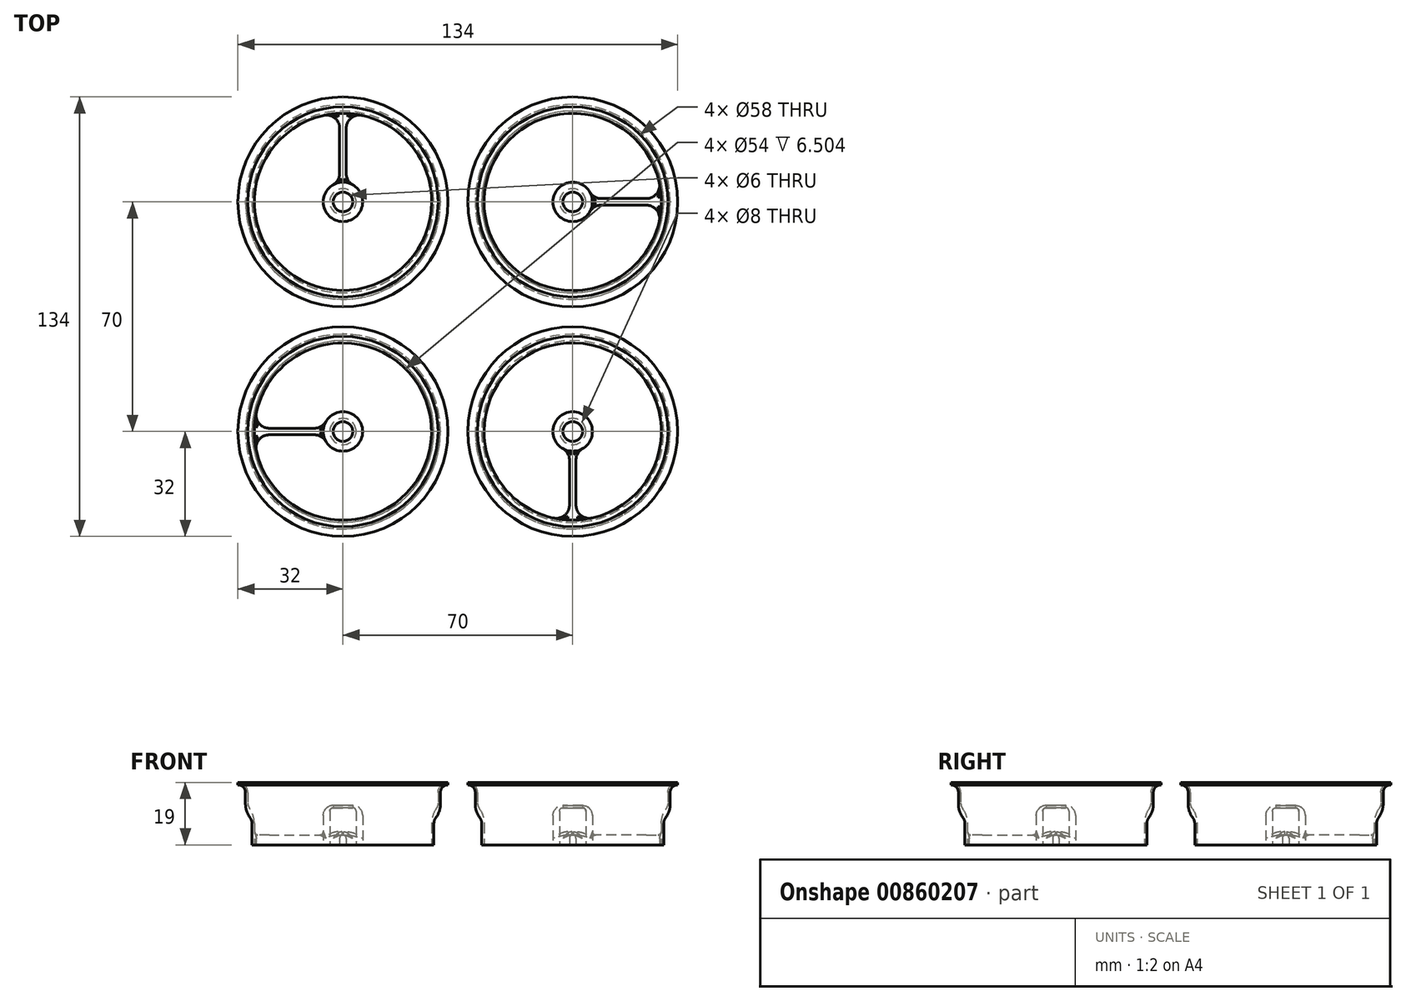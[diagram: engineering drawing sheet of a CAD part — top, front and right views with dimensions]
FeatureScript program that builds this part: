
annotation { "Feature Type Name" : "Feature", "Feature Type Description" : "" }
export const myFeature = defineFeature(function(context is Context, id is Id, definition is map)
    precondition{}
    {
        {
            var Q0;
            Q0=qCreatedBy(makeId("Front.planeOp"),FACE);
            var sketch = newSketch(context, id + "F0", { "sketchPlane" : qUnion([Q0])});
            skLineSegment(sketch, "E0", {"start": v(27, -5) * mm, "end": v(27, 5) * mm});
            skLineSegment(sketch, "E1", {"start": v(27, 5) * mm, "end": v(29, 5) * mm});
            skLineSegment(sketch, "E2", {"start": v(29, 5) * mm, "end": v(29, 11) * mm});
            skPoint(sketch, "E3", {"position": v(27, 0) * mm});
            skArc(sketch, "E4", {"start": v(32, 14) * mm, "mid": v(29.88, 13.12) * mm, "end": v(29, 11) * mm});
            skLineSegment(sketch, "E5.0", {"start": v(29.7, 4.3) * mm, "end": v(29.7, 11) * mm});
            skLineSegment(sketch, "E5.1", {"start": v(27.7, 4.3) * mm, "end": v(29.7, 4.3) * mm});
            skLineSegment(sketch, "E5.2", {"start": v(27.7, -5) * mm, "end": v(27.7, 4.3) * mm});
            skArc(sketch, "E6.0", {"start": v(32, 13.3) * mm, "mid": v(30.37, 12.63) * mm, "end": v(29.7, 11) * mm});
            skLineSegment(sketch, "E7", {"start": v(32, 14) * mm, "end": v(32, 13.3) * mm});
            skLineSegment(sketch, "E8", {"start": v(27, -5) * mm, "end": v(27.7, -5) * mm});
            skLineSegment(sketch, "E9.top", {"start": v(4, -5) * mm, "end": v(6, -5) * mm});
            skLineSegment(sketch, "E9.left", {"start": v(4, 5.3) * mm, "end": v(4, -5) * mm});
            skLineSegment(sketch, "E9.right", {"start": v(6, 7) * mm, "end": v(6, -5) * mm});
            skLineSegment(sketch, "E10", {"start": v(3, 6.3) * mm, "end": v(3, 6.3) * mm});
            skLineSegment(sketch, "E11", {"start": v(3, 6.3) * mm, "end": v(3, 7) * mm});
            skLineSegment(sketch, "E12", {"start": v(3, 7) * mm, "end": v(6, 7) * mm});
            skPoint(sketch, "E13.visualSharp", {"position": v(4, 6.3) * mm});
            skArc(sketch, "E13.filletArc", {"start": v(4, 5.3) * mm, "mid": v(3.7, 6) * mm, "end": v(3, 6.3) * mm});
            skLineSegment(sketch, "E14", {"start": v(0, 0) * mm, "end": v(0, 15.9) * mm, "construction": true});
            skSolve(sketch);
        }
        {
            var Q0;
            Q0 = qSketchRegion(id + "F0", true);
            var Q1;
            Q1=sQuery(id+"F0.wireOp",EDGE,"E14");
            revolve(context, id + "F1", {"surfaceOperationType" : NewSurfaceOperationType.NEW, "entities" : qUnion([Q0]), "axis" : qUnion([Q1]), "revolveType" : RevolveType.FULL});
        }
        {
            var Q0;
            Q0=makeQuery(id+"F1.opRevolve","SWEPT_EDGE",EDGE,{"disambiguationData":[OSD([sQuery(id+"F0.wireOp",EDGE,"E5.1"),sQuery(id+"F0.wireOp",EDGE,"E5.2")])]});
            var Q1;
            Q1=makeQuery(id+"F1.opRevolve","SWEPT_EDGE",EDGE,{"disambiguationData":[OSD([sQuery(id+"F0.wireOp",EDGE,"E1"),sQuery(id+"F0.wireOp",EDGE,"E2")])]});
            fillet(context, id + "F2", {"entities" : qUnion([Q0, Q1]), "radius" : 3 * mm, "tangentPropagation" : true, "allowEdgeOverflow" : false});
        }
        {
            var Q0;
            Q0=makeQuery(id+"F2.opFillet","BLEND_EDGE",EDGE,{"blendedFrom":[makeQuery(id+"F1.opRevolve","SWEPT_EDGE",EDGE,{"disambiguationData":[OSD([sQuery(id+"F0.wireOp",EDGE,"E5.1"),sQuery(id+"F0.wireOp",EDGE,"E5.2")])]}),makeQuery(id+"F1.opRevolve","SWEPT_FACE",FACE,{"disambiguationData":[OSD([sQuery(id+"F0.wireOp",EDGE,"E5.0")])]})],"blendedInto":[makeQuery(id+"F1.opRevolve","SWEPT_FACE",FACE,{"disambiguationData":[OSD([sQuery(id+"F0.wireOp",EDGE,"E5.0")])]})]});
            fillet(context, id + "F3", {"entities" : qUnion([Q0]), "radius" : 7 * mm, "tangentPropagation" : true, "allowEdgeOverflow" : false});
        }
        {
            var Q0;
            Q0=makeQuery(id+"F2.opFillet","BLEND_EDGE",EDGE,{"blendedFrom":[makeQuery(id+"F1.opRevolve","SWEPT_EDGE",EDGE,{"disambiguationData":[OSD([sQuery(id+"F0.wireOp",EDGE,"E1"),sQuery(id+"F0.wireOp",EDGE,"E2")])]}),makeQuery(id+"F1.opRevolve","SWEPT_FACE",FACE,{"disambiguationData":[OSD([sQuery(id+"F0.wireOp",EDGE,"E0")])]})],"blendedInto":[makeQuery(id+"F1.opRevolve","SWEPT_FACE",FACE,{"disambiguationData":[OSD([sQuery(id+"F0.wireOp",EDGE,"E0")])]})]});
            fillet(context, id + "F4", {"entities" : qUnion([Q0]), "radius" : 8 * mm, "tangentPropagation" : true, "allowEdgeOverflow" : false});
        }
        {
            var Q0;
            Q0=makeQuery(id+"F1.opRevolve","SWEPT_FACE",FACE,{"disambiguationData":[OSD([sQuery(id+"F0.wireOp",EDGE,"E9.top")])]});
            var sketch = newSketch(context, id + "F5", { "sketchPlane" : qUnion([Q0])});
            skArc(sketch, "E15", {"start": v(-1, -27.48) * mm, "mid": v(0, -27.5) * mm, "end": v(1, -27.48) * mm});
            skLineSegment(sketch, "E16", {"start": v(1, -27.48) * mm, "end": v(1, -5) * mm});
            skLineSegment(sketch, "E17", {"start": v(1, -5) * mm, "end": v(-1, -5) * mm});
            skLineSegment(sketch, "E18", {"start": v(-1, -5) * mm, "end": v(-1, -27.48) * mm});
            skPoint(sketch, "E19", {"position": v(0, -5) * mm});
            skSolve(sketch);
        }
        {
            var Q0;
            Q0 = qSketchRegion(id + "F5", true);
            extrude(context, id + "F6", {"entities" : qUnion([Q0]), "operationType" : NewBodyOperationType.ADD, "oppositeDirection" : true, "depth" : 3 * mm, "offsetDistance" : 25 * mm});
        }
        {
            var Q0;
            Q0=makeQuery(id+"F1.opRevolve","SWEPT_EDGE",EDGE,{"disambiguationData":[OSD([sQuery(id+"F0.wireOp",EDGE,"E9.right"),sQuery(id+"F0.wireOp",EDGE,"E12")])]});
            fillet(context, id + "F7", {"entities" : qUnion([Q0]), "radius" : 3 * mm, "tangentPropagation" : true, "allowEdgeOverflow" : false});
        }
        {
            var Q0;
            Q0=makeQuery(id+"FkhiXu6ylIL1KKB_1.2.F6.boolean.opBoolean","INTERSECT",EDGE,{"derivedFrom":[makeQuery(id+"F1.opRevolve","SWEPT_FACE",FACE,{"disambiguationData":[OSD([sQuery(id+"F0.wireOp",EDGE,"E0")])]}),makeQuery(id+"FkhiXu6ylIL1KKB_1.2.F6.opExtrude","SWEPT_FACE",FACE,{"disambiguationData":[OSD([sQuery(id+"F5.wireOp",EDGE,"E16")])]})]});
            var Q1;
            Q1=makeQuery(id+"FkhiXu6ylIL1KKB_1.2.F6.boolean.opBoolean","INTERSECT",EDGE,{"derivedFrom":[makeQuery(id+"F1.opRevolve","SWEPT_FACE",FACE,{"disambiguationData":[OSD([sQuery(id+"F0.wireOp",EDGE,"E0")])]}),makeQuery(id+"FkhiXu6ylIL1KKB_1.2.F6.opExtrude","SWEPT_FACE",FACE,{"disambiguationData":[OSD([sQuery(id+"F5.wireOp",EDGE,"E18")])]})]});
            var Q2;
            Q2=makeQuery(id+"F6.boolean.opBoolean","INTERSECT",EDGE,{"derivedFrom":[makeQuery(id+"F1.opRevolve","SWEPT_FACE",FACE,{"disambiguationData":[OSD([sQuery(id+"F0.wireOp",EDGE,"E0")])]}),makeQuery(id+"F6.opExtrude","SWEPT_FACE",FACE,{"disambiguationData":[OSD([sQuery(id+"F5.wireOp",EDGE,"E18")])]})]});
            var Q3;
            Q3=makeQuery(id+"FkhiXu6ylIL1KKB_1.1.F6.boolean.opBoolean","INTERSECT",EDGE,{"derivedFrom":[makeQuery(id+"F1.opRevolve","SWEPT_FACE",FACE,{"disambiguationData":[OSD([sQuery(id+"F0.wireOp",EDGE,"E9.right")])]}),makeQuery(id+"FkhiXu6ylIL1KKB_1.1.F6.opExtrude","SWEPT_FACE",FACE,{"disambiguationData":[OSD([sQuery(id+"F5.wireOp",EDGE,"E18")])]})]});
            var Q4;
            Q4=makeQuery(id+"FkhiXu6ylIL1KKB_1.2.F6.boolean.opBoolean","INTERSECT",EDGE,{"derivedFrom":[makeQuery(id+"F1.opRevolve","SWEPT_FACE",FACE,{"disambiguationData":[OSD([sQuery(id+"F0.wireOp",EDGE,"E9.right")])]}),makeQuery(id+"FkhiXu6ylIL1KKB_1.2.F6.opExtrude","SWEPT_FACE",FACE,{"disambiguationData":[OSD([sQuery(id+"F5.wireOp",EDGE,"E16")])]})]});
            var Q5;
            Q5=makeQuery(id+"FkhiXu6ylIL1KKB_1.2.F6.boolean.opBoolean","INTERSECT",EDGE,{"derivedFrom":[makeQuery(id+"F1.opRevolve","SWEPT_FACE",FACE,{"disambiguationData":[OSD([sQuery(id+"F0.wireOp",EDGE,"E9.right")])]}),makeQuery(id+"FkhiXu6ylIL1KKB_1.2.F6.opExtrude","SWEPT_FACE",FACE,{"disambiguationData":[OSD([sQuery(id+"F5.wireOp",EDGE,"E18")])]})]});
            var Q6;
            Q6=makeQuery(id+"F6.boolean.opBoolean","INTERSECT",EDGE,{"derivedFrom":[makeQuery(id+"F1.opRevolve","SWEPT_FACE",FACE,{"disambiguationData":[OSD([sQuery(id+"F0.wireOp",EDGE,"E9.right")])]}),makeQuery(id+"F6.opExtrude","SWEPT_FACE",FACE,{"disambiguationData":[OSD([sQuery(id+"F5.wireOp",EDGE,"E16")])]})]});
            var Q7;
            Q7=makeQuery(id+"F6.boolean.opBoolean","INTERSECT",EDGE,{"derivedFrom":[makeQuery(id+"F1.opRevolve","SWEPT_FACE",FACE,{"disambiguationData":[OSD([sQuery(id+"F0.wireOp",EDGE,"E9.right")])]}),makeQuery(id+"F6.opExtrude","SWEPT_FACE",FACE,{"disambiguationData":[OSD([sQuery(id+"F5.wireOp",EDGE,"E18")])]})]});
            var Q8;
            Q8=makeQuery(id+"FkhiXu6ylIL1KKB_1.1.F6.boolean.opBoolean","INTERSECT",EDGE,{"derivedFrom":[makeQuery(id+"F1.opRevolve","SWEPT_FACE",FACE,{"disambiguationData":[OSD([sQuery(id+"F0.wireOp",EDGE,"E9.right")])]}),makeQuery(id+"FkhiXu6ylIL1KKB_1.1.F6.opExtrude","SWEPT_FACE",FACE,{"disambiguationData":[OSD([sQuery(id+"F5.wireOp",EDGE,"E16")])]})]});
            var Q9;
            Q9=makeQuery(id+"F6.boolean.opBoolean","INTERSECT",EDGE,{"derivedFrom":[makeQuery(id+"F1.opRevolve","SWEPT_FACE",FACE,{"disambiguationData":[OSD([sQuery(id+"F0.wireOp",EDGE,"E0")])]}),makeQuery(id+"F6.opExtrude","SWEPT_FACE",FACE,{"disambiguationData":[OSD([sQuery(id+"F5.wireOp",EDGE,"E16")])]})]});
            var Q10;
            Q10=makeQuery(id+"FkhiXu6ylIL1KKB_1.1.F6.boolean.opBoolean","INTERSECT",EDGE,{"derivedFrom":[makeQuery(id+"F1.opRevolve","SWEPT_FACE",FACE,{"disambiguationData":[OSD([sQuery(id+"F0.wireOp",EDGE,"E0")])]}),makeQuery(id+"FkhiXu6ylIL1KKB_1.1.F6.opExtrude","SWEPT_FACE",FACE,{"disambiguationData":[OSD([sQuery(id+"F5.wireOp",EDGE,"E18")])]})]});
            var Q11;
            Q11=makeQuery(id+"FkhiXu6ylIL1KKB_1.1.F6.boolean.opBoolean","INTERSECT",EDGE,{"derivedFrom":[makeQuery(id+"F1.opRevolve","SWEPT_FACE",FACE,{"disambiguationData":[OSD([sQuery(id+"F0.wireOp",EDGE,"E0")])]}),makeQuery(id+"FkhiXu6ylIL1KKB_1.1.F6.opExtrude","SWEPT_FACE",FACE,{"disambiguationData":[OSD([sQuery(id+"F5.wireOp",EDGE,"E16")])]})]});
            var Q12;
            Q12=makeQuery(id+"FkhiXu6ylIL1KKB_1.3.F6.boolean.opBoolean","INTERSECT",EDGE,{"derivedFrom":[makeQuery(id+"F1.opRevolve","SWEPT_FACE",FACE,{"disambiguationData":[OSD([sQuery(id+"F0.wireOp",EDGE,"E0")])]}),makeQuery(id+"FkhiXu6ylIL1KKB_1.3.F6.opExtrude","SWEPT_FACE",FACE,{"disambiguationData":[OSD([sQuery(id+"F5.wireOp",EDGE,"E18")])]})]});
            var Q13;
            Q13=makeQuery(id+"FkhiXu6ylIL1KKB_1.3.F6.boolean.opBoolean","INTERSECT",EDGE,{"derivedFrom":[makeQuery(id+"F1.opRevolve","SWEPT_FACE",FACE,{"disambiguationData":[OSD([sQuery(id+"F0.wireOp",EDGE,"E0")])]}),makeQuery(id+"FkhiXu6ylIL1KKB_1.3.F6.opExtrude","SWEPT_FACE",FACE,{"disambiguationData":[OSD([sQuery(id+"F5.wireOp",EDGE,"E16")])]})]});
            var Q14;
            Q14=makeQuery(id+"FkhiXu6ylIL1KKB_1.3.F6.boolean.opBoolean","INTERSECT",EDGE,{"derivedFrom":[makeQuery(id+"F1.opRevolve","SWEPT_FACE",FACE,{"disambiguationData":[OSD([sQuery(id+"F0.wireOp",EDGE,"E9.right")])]}),makeQuery(id+"FkhiXu6ylIL1KKB_1.3.F6.opExtrude","SWEPT_FACE",FACE,{"disambiguationData":[OSD([sQuery(id+"F5.wireOp",EDGE,"E16")])]})]});
            var Q15;
            Q15=makeQuery(id+"FkhiXu6ylIL1KKB_1.3.F6.boolean.opBoolean","INTERSECT",EDGE,{"derivedFrom":[makeQuery(id+"F1.opRevolve","SWEPT_FACE",FACE,{"disambiguationData":[OSD([sQuery(id+"F0.wireOp",EDGE,"E9.right")])]}),makeQuery(id+"FkhiXu6ylIL1KKB_1.3.F6.opExtrude","SWEPT_FACE",FACE,{"disambiguationData":[OSD([sQuery(id+"F5.wireOp",EDGE,"E18")])]})]});
            fillet(context, id + "F8", {"entities" : qUnion([Q0, Q1, Q2, Q3, Q4, Q5, Q6, Q7, Q8, Q9, Q10, Q11, Q12, Q13, Q14, Q15]), "radius" : 4 * mm, "tangentPropagation" : true, "allowEdgeOverflow" : false});
        }
        {
            var Q0;
            Q0=makeQuery(id+"FkhiXu6ylIL1KKB_1.1.F6.opExtrude","CAP_FACE",FACE,{"disambiguationData":[OSD([sQuery(id+"F5.wireOp",EDGE,"E15"),sQuery(id+"F5.wireOp",EDGE,"E16"),sQuery(id+"F5.wireOp",EDGE,"E17"),sQuery(id+"F5.wireOp",EDGE,"E18")])],"isStart":false});
            var Q1;
            Q1=makeQuery(id+"F6.opExtrude","CAP_FACE",FACE,{"disambiguationData":[OSD([sQuery(id+"F5.wireOp",EDGE,"E15"),sQuery(id+"F5.wireOp",EDGE,"E16"),sQuery(id+"F5.wireOp",EDGE,"E17"),sQuery(id+"F5.wireOp",EDGE,"E18")])],"isStart":false});
            var Q2;
            Q2=makeQuery(id+"FkhiXu6ylIL1KKB_1.2.F6.opExtrude","CAP_FACE",FACE,{"disambiguationData":[OSD([sQuery(id+"F5.wireOp",EDGE,"E15"),sQuery(id+"F5.wireOp",EDGE,"E16"),sQuery(id+"F5.wireOp",EDGE,"E17"),sQuery(id+"F5.wireOp",EDGE,"E18")])],"isStart":false});
            var Q3;
            Q3=makeQuery(id+"FkhiXu6ylIL1KKB_1.3.F6.opExtrude","CAP_FACE",FACE,{"disambiguationData":[OSD([sQuery(id+"F5.wireOp",EDGE,"E15"),sQuery(id+"F5.wireOp",EDGE,"E16"),sQuery(id+"F5.wireOp",EDGE,"E17"),sQuery(id+"F5.wireOp",EDGE,"E18")])],"isStart":false});
            fillet(context, id + "F9", {"entities" : qUnion([Q0, Q1, Q2, Q3]), "radius" : 1 * mm, "tangentPropagation" : true, "allowEdgeOverflow" : false});
        }
        {
            var Q0;
            Q0=qCreatedBy(makeId("Right.planeOp"),FACE);
            cPlane(context, id + "F10", {"entities" : qUnion([Q0]), "cplaneType" : CPlaneType.OFFSET, "offset" : 35 * mm, "width" : 150 * mm, "height" : 150 * mm});
        }
        {
            var Q0;
            Q0=qCreatedBy(makeId("Front.planeOp"),FACE);
            cPlane(context, id + "F11", {"entities" : qUnion([Q0]), "cplaneType" : CPlaneType.OFFSET, "offset" : 35 * mm, "width" : 150 * mm, "height" : 150 * mm});
        }
        {
            var Q0;
            Q0=qCreatedBy(id+"F10.planeOp",FACE);
            var sketch = newSketch(context, id + "F12", { "sketchPlane" : qUnion([Q0])});
            skLineSegment(sketch, "E20", {"start": v(-35, 0) * mm, "end": v(-35, 88.37) * mm, "construction": true});
            skSolve(sketch);
        }
        {
            var Q0;
            Q0=makeQuery(id+"F1.opRevolve","SWEPT_BODY",BODY,{"disambiguationData":[OSD([sQuery(id+"F0.wireOp",EDGE,"E0"),sQuery(id+"F0.wireOp",EDGE,"E1"),sQuery(id+"F0.wireOp",EDGE,"E2"),sQuery(id+"F0.wireOp",EDGE,"E4"),sQuery(id+"F0.wireOp",EDGE,"E5.0"),sQuery(id+"F0.wireOp",EDGE,"E5.1"),sQuery(id+"F0.wireOp",EDGE,"E5.2"),sQuery(id+"F0.wireOp",EDGE,"E6.0"),sQuery(id+"F0.wireOp",EDGE,"E7"),sQuery(id+"F0.wireOp",EDGE,"E8")])]});
            var Q1;
            Q1=sQuery(id+"F12.wireOp",EDGE,"E20");
            circularPattern(context, id + "F13", {"entities" : qUnion([Q0]), "axis" : qUnion([Q1]), "angle" : 360 * degree, "instanceCount" : 4, "equalSpace" : true});
        }
    });
